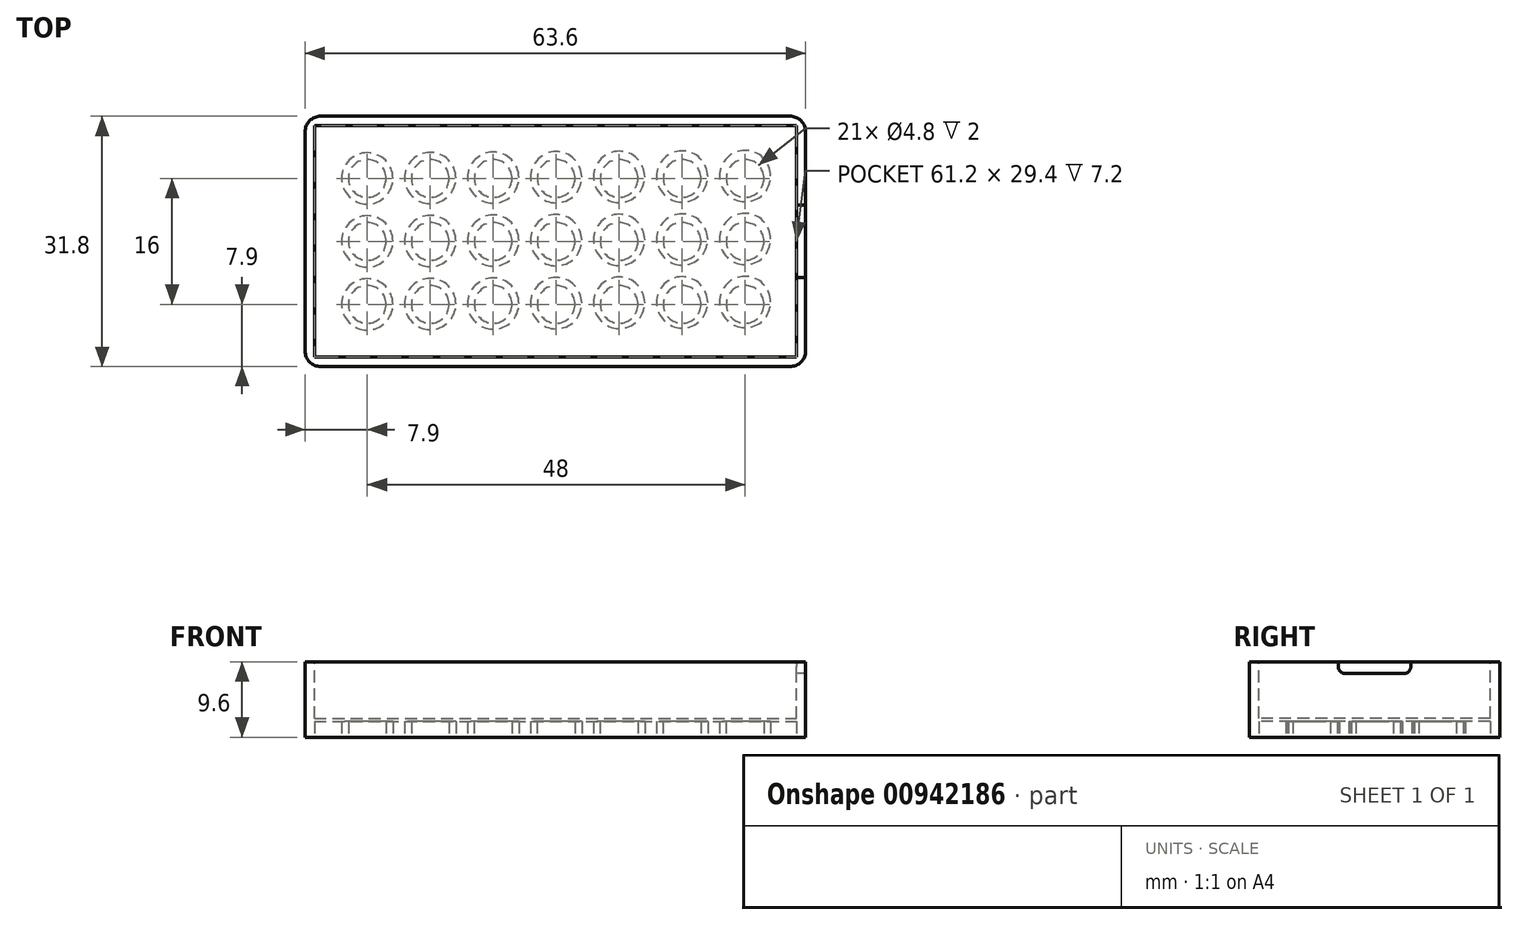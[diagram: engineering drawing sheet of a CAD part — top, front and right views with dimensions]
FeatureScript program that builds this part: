
annotation { "Feature Type Name" : "Feature", "Feature Type Description" : "" }
export const myFeature = defineFeature(function(context is Context, id is Id, definition is map)
    precondition{}
    {
        {
            var Q0;
            Q0=qCreatedBy(makeId("Top.planeOp"),FACE);
            var sketch = newSketch(context, id + "F0", { "sketchPlane" : qUnion([Q0])});
            skLineSegment(sketch, "E0.bottom", {"start": v(-31.8, 15.9) * mm, "end": v(31.8, 15.9) * mm});
            skLineSegment(sketch, "E0.top", {"start": v(-31.8, -15.9) * mm, "end": v(31.8, -15.9) * mm});
            skLineSegment(sketch, "E0.left", {"start": v(-31.8, 15.9) * mm, "end": v(-31.8, -15.9) * mm});
            skLineSegment(sketch, "E0.right", {"start": v(31.8, 15.9) * mm, "end": v(31.8, -15.9) * mm});
            skSolve(sketch);
        }
        {
            var Q0;
            Q0=qSketchRegion(id+"F0",true);
            extrude(context, id + "F1", {"entities" : qUnion([Q0]), "depth" : 9.6 * mm, "offsetDistance" : 25 * mm});
        }
        {
            var Q0;
            Q0=qCreatedBy(makeId("Top.planeOp"),FACE);
            var sketch = newSketch(context, id + "F2", { "sketchPlane" : qUnion([Q0])});
            skLineSegment(sketch, "E1.bottom", {"start": v(-30.6, 14.7) * mm, "end": v(30.6, 14.7) * mm});
            skLineSegment(sketch, "E1.top", {"start": v(-30.6, -14.7) * mm, "end": v(30.6, -14.7) * mm});
            skLineSegment(sketch, "E1.left", {"start": v(-30.6, 14.7) * mm, "end": v(-30.6, -14.7) * mm});
            skLineSegment(sketch, "E1.right", {"start": v(30.6, 14.7) * mm, "end": v(30.6, -14.7) * mm});
            skSolve(sketch);
        }
        {
            var Q0;
            Q0=qSketchRegion(id+"F2",true);
            extrude(context, id + "F3", {"entities" : qUnion([Q0]), "operationType" : NewBodyOperationType.REMOVE, "depth" : 2 * mm, "offsetDistance" : 25 * mm});
        }
        {
            var Q0;
            Q0=makeQuery(id+"F1.opExtrude","SWEPT_EDGE",EDGE,{"disambiguationData":[OSD([sQuery(id+"F0.wireOp",EDGE,"E0.top"),sQuery(id+"F0.wireOp",EDGE,"E0.left")])]});
            var Q1;
            Q1=makeQuery(id+"F1.opExtrude","SWEPT_EDGE",EDGE,{"disambiguationData":[OSD([sQuery(id+"F0.wireOp",EDGE,"E0.bottom"),sQuery(id+"F0.wireOp",EDGE,"E0.left")])]});
            var Q2;
            Q2=makeQuery(id+"F1.opExtrude","SWEPT_EDGE",EDGE,{"disambiguationData":[OSD([sQuery(id+"F0.wireOp",EDGE,"E0.bottom"),sQuery(id+"F0.wireOp",EDGE,"E0.right")])]});
            var Q3;
            Q3=makeQuery(id+"F1.opExtrude","SWEPT_EDGE",EDGE,{"disambiguationData":[OSD([sQuery(id+"F0.wireOp",EDGE,"E0.top"),sQuery(id+"F0.wireOp",EDGE,"E0.right")])]});
            fillet(context, id + "F4", {"entities" : qUnion([Q0, Q1, Q2, Q3]), "radius" : 2 * mm, "tangentPropagation" : true, "allowEdgeOverflow" : false});
        }
        {
            var Q0;
            Q0=qCreatedBy(makeId("Top.planeOp"),FACE);
            cPlane(context, id + "F5", {"entities" : qUnion([Q0]), "cplaneType" : CPlaneType.OFFSET, "offset" : 9.6 * mm, "width" : 150 * mm, "height" : 150 * mm});
        }
        {
            var Q0;
            Q0=qCreatedBy(id+"F5.planeOp",FACE);
            var sketch = newSketch(context, id + "F6", { "sketchPlane" : qUnion([Q0])});
            skLineSegment(sketch, "E2.bottom", {"start": v(-30.6, 14.7) * mm, "end": v(30.6, 14.7) * mm});
            skLineSegment(sketch, "E2.top", {"start": v(-30.6, -14.7) * mm, "end": v(30.6, -14.7) * mm});
            skLineSegment(sketch, "E2.left", {"start": v(-30.6, 14.7) * mm, "end": v(-30.6, -14.7) * mm});
            skLineSegment(sketch, "E2.right", {"start": v(30.6, 14.7) * mm, "end": v(30.6, -14.7) * mm});
            skSolve(sketch);
        }
        {
            var Q0;
            Q0=qSketchRegion(id+"F6",true);
            var Q1;
            Q1=sQuery(id+"F6.wireOp",EDGE,"E2.bottom");
            var Q2;
            Q2=sQuery(id+"F6.wireOp",EDGE,"E2.top");
            var Q3;
            Q3=sQuery(id+"F6.wireOp",EDGE,"E2.left");
            var Q4;
            Q4=sQuery(id+"F6.wireOp",EDGE,"E2.right");
            extrude(context, id + "F7", {"entities" : qUnion([Q0]), "operationType" : NewBodyOperationType.REMOVE, "surfaceEntities" : qUnion([Q1, Q2, Q3, Q4]), "oppositeDirection" : true, "depth" : 7.2 * mm, "offsetDistance" : 25 * mm});
        }
        {
            var Q0;
            Q0=qCreatedBy(makeId("Top.planeOp"),FACE);
            var sketch = newSketch(context, id + "F8", { "sketchPlane" : qUnion([Q0])});
            skCircle(sketch, "E3.1.1.0", {"center": v(-23.9, -8) * mm, "radius": 3.26 * mm});
            skCircle(sketch, "E4.0.1.0", {"center": v(-23.9, 0) * mm, "radius": 3.26 * mm});
            skCircle(sketch, "E4.0.2.0", {"center": v(-23.9, 8) * mm, "radius": 3.26 * mm});
            skCircle(sketch, "E4.1.0.0", {"center": v(-15.9, -7.95) * mm, "radius": 3.26 * mm});
            skCircle(sketch, "E4.1.1.0", {"center": v(-15.9, 0.05) * mm, "radius": 3.26 * mm});
            skCircle(sketch, "E4.1.2.0", {"center": v(-15.9, 8.05) * mm, "radius": 3.26 * mm});
            skCircle(sketch, "E4.2.0.0", {"center": v(-7.9, -7.9) * mm, "radius": 3.26 * mm});
            skCircle(sketch, "E4.2.1.0", {"center": v(-7.9, 0.1) * mm, "radius": 3.26 * mm});
            skCircle(sketch, "E4.2.2.0", {"center": v(-7.9, 8.1) * mm, "radius": 3.26 * mm});
            skLineSegment(sketch, "E4.direction1", {"start": v(-23.9, -8) * mm, "end": v(-15.9, -7.95) * mm, "construction": true});
            skLineSegment(sketch, "E4.direction2", {"start": v(-23.9, -8) * mm, "end": v(-23.9, 0) * mm, "construction": true});
            skCircle(sketch, "E5.0.3.0", {"center": v(0.1, -7.85) * mm, "radius": 3.26 * mm});
            skCircle(sketch, "E5.0.3.1", {"center": v(0.1, 0.15) * mm, "radius": 3.26 * mm});
            skCircle(sketch, "E5.0.3.2", {"center": v(0.1, 8.15) * mm, "radius": 3.26 * mm});
            skCircle(sketch, "E5.0.4.0", {"center": v(8.1, -7.8) * mm, "radius": 3.26 * mm});
            skCircle(sketch, "E5.0.4.1", {"center": v(8.1, 0.2) * mm, "radius": 3.26 * mm});
            skCircle(sketch, "E5.0.4.2", {"center": v(8.1, 8.2) * mm, "radius": 3.26 * mm});
            skCircle(sketch, "E5.0.5.0", {"center": v(16.1, -7.75) * mm, "radius": 3.26 * mm});
            skCircle(sketch, "E5.0.5.1", {"center": v(16.1, 0.25) * mm, "radius": 3.26 * mm});
            skCircle(sketch, "E5.0.5.2", {"center": v(16.1, 8.25) * mm, "radius": 3.26 * mm});
            skCircle(sketch, "E6.0.6.0", {"center": v(24.1, -7.7) * mm, "radius": 3.26 * mm});
            skCircle(sketch, "E6.0.6.1", {"center": v(24.1, 0.3) * mm, "radius": 3.26 * mm});
            skCircle(sketch, "E6.0.6.2", {"center": v(24.1, 8.3) * mm, "radius": 3.26 * mm});
            skSolve(sketch);
        }
        {
            var Q0;
            Q0=qCreatedBy(makeId("Top.planeOp"),FACE);
            var sketch = newSketch(context, id + "F9", { "sketchPlane" : qUnion([Q0])});
            skCircle(sketch, "E7", {"center": v(-23.9, -8) * mm, "radius": 2.4 * mm});
            skCircle(sketch, "E8.0.1.0", {"center": v(-23.9, 0) * mm, "radius": 2.4 * mm});
            skCircle(sketch, "E8.0.2.0", {"center": v(-23.9, 8) * mm, "radius": 2.4 * mm});
            skCircle(sketch, "E8.1.0.0", {"center": v(-15.9, -8) * mm, "radius": 2.4 * mm});
            skCircle(sketch, "E8.1.1.0", {"center": v(-15.9, 0) * mm, "radius": 2.4 * mm});
            skCircle(sketch, "E8.1.2.0", {"center": v(-15.9, 8) * mm, "radius": 2.4 * mm});
            skCircle(sketch, "E8.2.0.0", {"center": v(-7.9, -8) * mm, "radius": 2.4 * mm});
            skCircle(sketch, "E8.2.1.0", {"center": v(-7.9, 0) * mm, "radius": 2.4 * mm});
            skCircle(sketch, "E8.2.2.0", {"center": v(-7.9, 8) * mm, "radius": 2.4 * mm});
            skLineSegment(sketch, "E8.direction1", {"start": v(-23.9, -8) * mm, "end": v(-15.9, -8) * mm, "construction": true});
            skLineSegment(sketch, "E8.direction2", {"start": v(-23.9, -8) * mm, "end": v(-23.9, 0) * mm, "construction": true});
            skCircle(sketch, "E9.0.3.0", {"center": v(0.1, -8) * mm, "radius": 2.4 * mm});
            skCircle(sketch, "E9.0.3.1", {"center": v(0.1, 0) * mm, "radius": 2.4 * mm});
            skCircle(sketch, "E9.0.3.2", {"center": v(0.1, 8) * mm, "radius": 2.4 * mm});
            skCircle(sketch, "E9.0.4.0", {"center": v(8.1, -8) * mm, "radius": 2.4 * mm});
            skCircle(sketch, "E9.0.4.1", {"center": v(8.1, 0) * mm, "radius": 2.4 * mm});
            skCircle(sketch, "E9.0.4.2", {"center": v(8.1, 8) * mm, "radius": 2.4 * mm});
            skCircle(sketch, "E9.0.5.0", {"center": v(16.1, -8) * mm, "radius": 2.4 * mm});
            skCircle(sketch, "E9.0.5.1", {"center": v(16.1, 0) * mm, "radius": 2.4 * mm});
            skCircle(sketch, "E9.0.5.2", {"center": v(16.1, 8) * mm, "radius": 2.4 * mm});
            skCircle(sketch, "E9.0.6.0", {"center": v(24.1, -8) * mm, "radius": 2.4 * mm});
            skCircle(sketch, "E9.0.6.1", {"center": v(24.1, 0) * mm, "radius": 2.4 * mm});
            skCircle(sketch, "E9.0.6.2", {"center": v(24.1, 8) * mm, "radius": 2.4 * mm});
            skSolve(sketch);
        }
        {
            var Q0;
            Q0=qSketchRegion(id+"F8",true);
            extrude(context, id + "F10", {"entities" : qUnion([Q0]), "operationType" : NewBodyOperationType.ADD, "depth" : 2.4 * mm, "offsetDistance" : 25 * mm});
        }
        {
            var Q0;
            Q0=qSketchRegion(id+"F9",true);
            extrude(context, id + "F11", {"entities" : qUnion([Q0]), "operationType" : NewBodyOperationType.REMOVE, "depth" : 2 * mm, "offsetDistance" : 25 * mm});
        }
        {
            var Q0;
            Q0=qCreatedBy(makeId("Right.planeOp"),FACE);
            var sketch = newSketch(context, id + "F12", { "sketchPlane" : qUnion([Q0])});
            skLineSegment(sketch, "E10.bottom", {"start": v(-3.72, 11.1) * mm, "end": v(3.7, 11.1) * mm});
            skLineSegment(sketch, "E10.top", {"start": v(-3.72, 8.1) * mm, "end": v(3.7, 8.1) * mm});
            skLineSegment(sketch, "E10.left", {"start": v(-4.62, 10.2) * mm, "end": v(-4.62, 9) * mm});
            skLineSegment(sketch, "E10.right", {"start": v(4.6, 10.2) * mm, "end": v(4.6, 9) * mm});
            skPoint(sketch, "E10.middle", {"position": v(0, 9.6) * mm});
            skPoint(sketch, "E11", {"position": v(-3.72, 10.2) * mm});
            skPoint(sketch, "E12", {"position": v(3.7, 10.2) * mm});
            skPoint(sketch, "E13", {"position": v(3.7, 9) * mm});
            skPoint(sketch, "E14", {"position": v(-3.72, 9) * mm});
            skArc(sketch, "E15", {"start": v(-3.72, 11.1) * mm, "mid": v(-4.35, 10.84) * mm, "end": v(-4.62, 10.2) * mm});
            skArc(sketch, "E16", {"start": v(-4.62, 9) * mm, "mid": v(-4.35, 8.36) * mm, "end": v(-3.72, 8.1) * mm});
            skArc(sketch, "E17", {"start": v(3.7, 8.1) * mm, "mid": v(4.34, 8.36) * mm, "end": v(4.6, 9) * mm});
            skPoint(sketch, "E18.orphan", {"position": v(4.6, 11.1) * mm});
            skPoint(sketch, "E19.orphan", {"position": v(4.6, 8.1) * mm});
            skPoint(sketch, "E20.orphan", {"position": v(-4.62, 8.1) * mm});
            skPoint(sketch, "E21.orphan", {"position": v(-4.62, 11.1) * mm});
            skArc(sketch, "E22.trimOffspring", {"start": v(4.6, 10.2) * mm, "mid": v(4.34, 10.84) * mm, "end": v(3.7, 11.1) * mm});
            skSolve(sketch);
        }
        {
            var Q0;
            Q0 = qSketchRegion(id + "F12", true);
            extrude(context, id + "F13", {"entities" : qUnion([Q0]), "operationType" : NewBodyOperationType.REMOVE, "depth" : 32 * mm, "offsetDistance" : 25 * mm});
        }
    });
